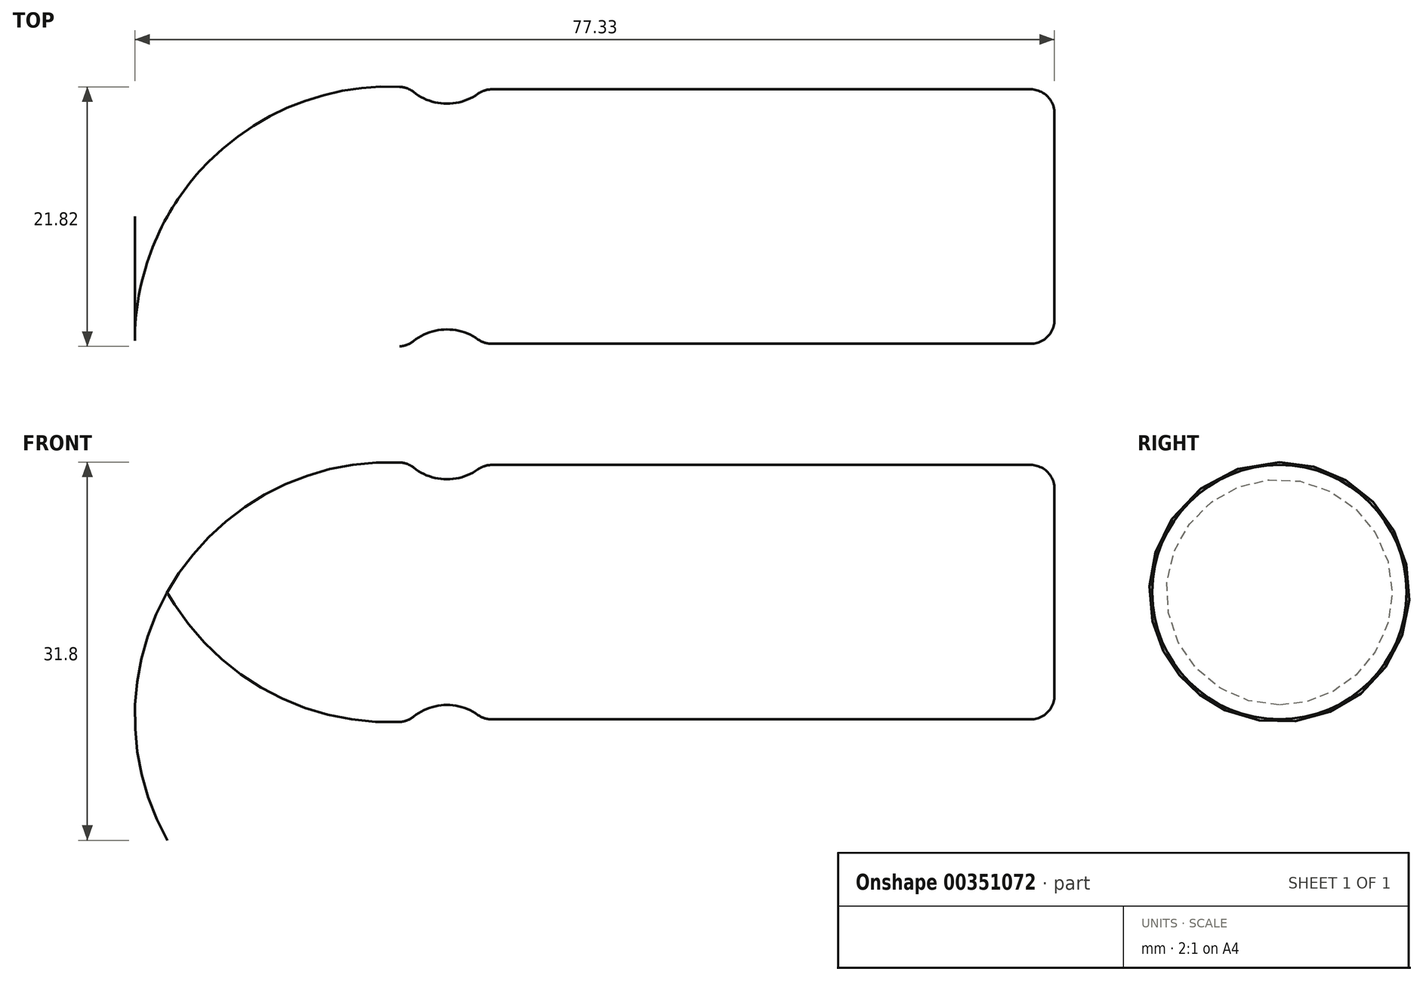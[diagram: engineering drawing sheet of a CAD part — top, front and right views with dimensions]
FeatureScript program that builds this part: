
annotation { "Feature Type Name" : "Feature", "Feature Type Description" : "" }
export const myFeature = defineFeature(function(context is Context, id is Id, definition is map)
    precondition{}
    {
        {
            var Q0;
            Q0=qCreatedBy(makeId("Front.planeOp"),FACE);
            var sketch = newSketch(context, id + "F0", { "sketchPlane" : qUnion([Q0])});
            skArc(sketch, "E0", {"start": v(20.29, 10.87) * mm, "mid": v(8.56, 8.4) * mm, "end": v(0, 0) * mm});
            skLineSegment(sketch, "E1", {"start": v(26.58, 10.7) * mm, "end": v(74.6, 10.7) * mm});
            skLineSegment(sketch, "E2", {"start": v(74.6, 10.7) * mm, "end": v(74.6, 0) * mm});
            skLineSegment(sketch, "E3", {"start": v(74.6, 0) * mm, "end": v(0, 0) * mm});
            skArc(sketch, "E4", {"start": v(20.29, 10.87) * mm, "mid": v(23.4, 9.5) * mm, "end": v(26.58, 10.7) * mm});
            skSolve(sketch);
        }
        {
            var Q0;
            Q0=makeQuery(id+"F0.imprint","IMPRINT",FACE,{"disambiguationData":[TD([[makeQuery(id+"F0.imprint","IMPRINT",EDGE,{"derivedFrom":sQuery(id+"F0.wireOp",EDGE,"E0")}),1.0]])]});
            var Q1;
            Q1=sQuery(id+"F0.wireOp",EDGE,"E3");
            revolve(context, id + "F1", {"entities" : qUnion([Q0]), "axis" : qUnion([Q1]), "revolveType" : RevolveType.FULL});
        }
        {
            var Q0;
            Q0=makeQuery(id+"F1.opRevolve","SWEPT_EDGE",EDGE,{"disambiguationData":[OSD([sQuery(id+"F0.wireOp",EDGE,"E0"),sQuery(id+"F0.wireOp",EDGE,"E4")])]});
            var Q1;
            Q1=makeQuery(id+"F1.opRevolve","SWEPT_EDGE",EDGE,{"disambiguationData":[OSD([sQuery(id+"F0.wireOp",EDGE,"E1"),sQuery(id+"F0.wireOp",EDGE,"E4")])]});
            var Q2;
            Q2=makeQuery(id+"F1.opRevolve","SWEPT_EDGE",EDGE,{"disambiguationData":[OSD([sQuery(id+"F0.wireOp",EDGE,"E1"),sQuery(id+"F0.wireOp",EDGE,"E2")])]});
            fillet(context, id + "F2", {"entities" : qUnion([Q0, Q1, Q2]), "radius" : 2 * mm, "tangentPropagation" : true, "allowEdgeOverflow" : false});
        }
    });
